# Revit family: FU_Inspec_Sunny_5-2
name_source: partatom
category: Furniture
units: mm (PartAtom-declared; Revit-internal decimal feet)

## family parameters
Always vertical = Yes
Cut with Voids When Loaded = No
OmniClass Number = 23.40.20.00
OmniClass Title = General Furniture and Specialties
Room Calculation Point = No
Shared = No
Work Plane-Based = No

## types (6) — shared parameters
Assembly Code = E2020
Keynote = 46.B
Manufacturer = Inspec
URL = https://inspecfurniture.com
zero-valued in all types: Default Elevation

## per-type parameters (varying)
| type | Description | Frame Material | Model | Seat Material |
| Sunny 5.1 - Graphite - Beige | Freestanding lounge chair with frame of steel tubing and fully upholstered seat | Epoxy - Powdercoats - Graphite | Sunny 5.1 | Fabric - Canvas - Beige |
| Sunny 5.2 - Chrome - Blue | Freestanding lounge chair with frame of steel tubing, arms and fully upholstered seat | Metal - Chrome - Polished | Sunny 5.2 | Fabric - Canvas - Blue |
| Sunny 5.2 - Graphite - Black | Freestanding lounge chair with frame of steel tubing, arms and fully upholstered seat | Epoxy - Powdercoats - Graphite | Sunny 5.2 | Fabric - Woven - Black |
| Sunny 5.1 - Chrome - Yellow | Freestanding lounge chair with frame of steel tubing and fully upholstered seat | Metal - Chrome - Polished | Sunny 5.1 | Fabric - Canvas - Yellow |
| Sunny 5.1 - White - White | Freestanding lounge chair with frame of steel tubing and fully upholstered seat | Epoxy - Powdercoats - White | Sunny 5.1 | Fabric - Canvas - White |
| Sunny 5.2 - Grey - Brown | Freestanding lounge chair with frame of steel tubing, arms and fully upholstered seat | Epoxy - Powdercoats - Gray | Sunny 5.2 | Fabric - Woven - Brown |

## geometry (parser evidence)
native form markers: Sweep x5
no freeform markers — native parametric forms only
